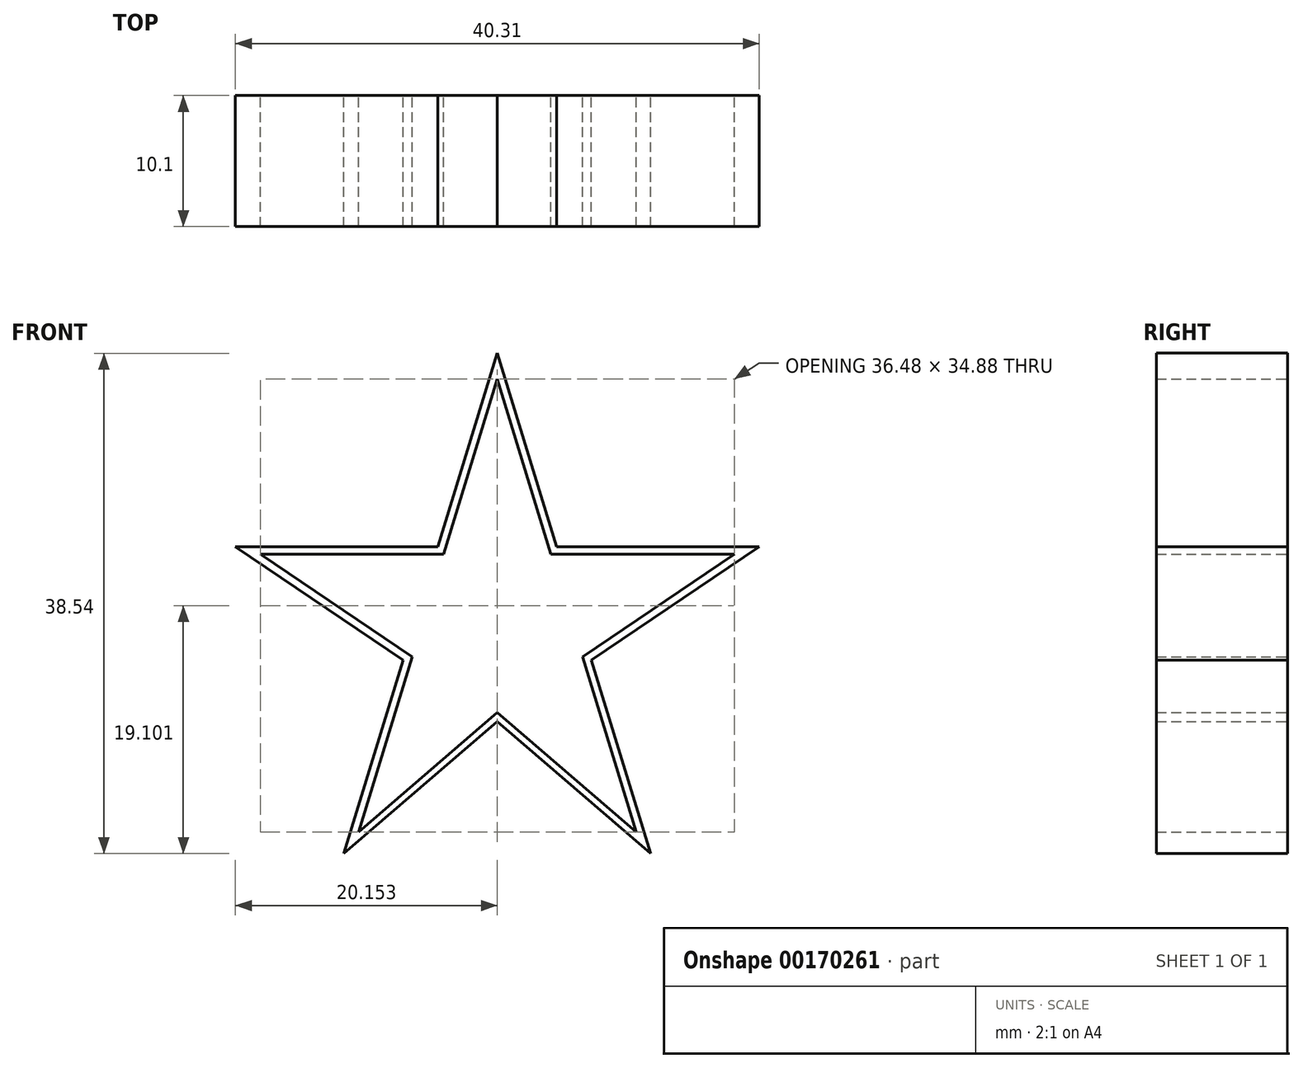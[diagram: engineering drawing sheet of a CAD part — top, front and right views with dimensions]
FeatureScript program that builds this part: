
annotation { "Feature Type Name" : "Feature", "Feature Type Description" : "" }
export const myFeature = defineFeature(function(context is Context, id is Id, definition is map)
    precondition{}
    {
        {
            var Q0;
            Q0=qCreatedBy(makeId("Front.planeOp"),FACE);
            var sketch = newSketch(context, id + "F0", { "sketchPlane" : qUnion([Q0])});
            skLineSegment(sketch, "E0", {"start": v(-37.38, 63.45) * mm, "end": v(-37.38, 61.45) * mm});
            skLineSegment(sketch, "E1", {"start": v(-37.38, 63.45) * mm, "end": v(-41.94, 48.55) * mm});
            skLineSegment(sketch, "E2", {"start": v(-37.38, 61.45) * mm, "end": v(-41.5, 47.96) * mm});
            skLineSegment(sketch, "E3", {"start": v(-41.94, 48.55) * mm, "end": v(-41.5, 47.96) * mm});
            skLineSegment(sketch, "E4", {"start": v(-41.94, 48.55) * mm, "end": v(-57.53, 48.55) * mm});
            skLineSegment(sketch, "E5", {"start": v(-55.62, 47.96) * mm, "end": v(-41.5, 47.96) * mm});
            skLineSegment(sketch, "E6", {"start": v(-49.74, 48.55) * mm, "end": v(-49.74, 47.96) * mm});
            skLineSegment(sketch, "E7", {"start": v(-39.66, 56) * mm, "end": v(-39.1, 55.83) * mm});
            skLineSegment(sketch, "E8", {"start": v(-55.62, 47.96) * mm, "end": v(-57.53, 48.55) * mm});
            skLineSegment(sketch, "E9.MirrorCS", {"start": v(-55.62, 47.96) * mm, "end": v(-43.93, 40.06) * mm});
            skLineSegment(sketch, "E10.MirrorCS", {"start": v(-44.62, 39.82) * mm, "end": v(-57.53, 48.55) * mm});
            skLineSegment(sketch, "E11.MirrorCS", {"start": v(-51.07, 44.18) * mm, "end": v(-50.75, 44.67) * mm});
            skLineSegment(sketch, "E12.MirrorCS", {"start": v(-44.62, 39.82) * mm, "end": v(-43.93, 40.06) * mm});
            skLineSegment(sketch, "E13.MirrorCS", {"start": v(-49.18, 24.91) * mm, "end": v(-44.62, 39.82) * mm});
            skLineSegment(sketch, "E14.MirrorCS", {"start": v(-48.06, 26.57) * mm, "end": v(-43.93, 40.06) * mm});
            skLineSegment(sketch, "E15", {"start": v(-49.18, 24.91) * mm, "end": v(-37.38, 35.1) * mm});
            skLineSegment(sketch, "E16.MirrorCS", {"start": v(-46.9, 32.37) * mm, "end": v(-46.34, 32.2) * mm});
            skLineSegment(sketch, "E17.MirrorCS", {"start": v(-49.18, 24.91) * mm, "end": v(-48.06, 26.57) * mm});
            skLineSegment(sketch, "E18", {"start": v(-37.38, 61.45) * mm, "end": v(-37.38, 35.1) * mm});
            skLineSegment(sketch, "E19", {"start": v(-48.06, 26.57) * mm, "end": v(-37.38, 35.79) * mm});
            skLineSegment(sketch, "E20", {"start": v(-42.4, 30.76) * mm, "end": v(-42.74, 31.16) * mm});
            skLineSegment(sketch, "E21.MirrorCS", {"start": v(-19.14, 47.96) * mm, "end": v(-17.22, 48.55) * mm});
            skLineSegment(sketch, "E22.MirrorCS", {"start": v(-25.57, 24.91) * mm, "end": v(-26.7, 26.57) * mm});
            skLineSegment(sketch, "E23.MirrorCS", {"start": v(-32.81, 48.55) * mm, "end": v(-33.25, 47.96) * mm});
            skLineSegment(sketch, "E24.MirrorCS", {"start": v(-30.14, 39.82) * mm, "end": v(-30.83, 40.06) * mm});
            skLineSegment(sketch, "E25.MirrorCS", {"start": v(-27.86, 32.37) * mm, "end": v(-28.42, 32.2) * mm});
            skLineSegment(sketch, "E26.MirrorCS", {"start": v(-35.1, 56) * mm, "end": v(-35.65, 55.83) * mm});
            skLineSegment(sketch, "E27.MirrorCS", {"start": v(-32.36, 30.76) * mm, "end": v(-32.01, 31.16) * mm});
            skLineSegment(sketch, "E28.MirrorCS", {"start": v(-25.02, 48.55) * mm, "end": v(-25.02, 47.96) * mm});
            skLineSegment(sketch, "E29.MirrorCS", {"start": v(-23.68, 44.18) * mm, "end": v(-24, 44.67) * mm});
            skLineSegment(sketch, "E30.MirrorCS", {"start": v(-19.14, 47.96) * mm, "end": v(-33.25, 47.96) * mm});
            skLineSegment(sketch, "E31.MirrorCS", {"start": v(-26.7, 26.57) * mm, "end": v(-37.38, 35.79) * mm});
            skLineSegment(sketch, "E32.MirrorCS", {"start": v(-26.7, 26.57) * mm, "end": v(-30.83, 40.06) * mm});
            skLineSegment(sketch, "E33.MirrorCS", {"start": v(-30.14, 39.82) * mm, "end": v(-17.22, 48.55) * mm});
            skLineSegment(sketch, "E34.MirrorCS", {"start": v(-37.38, 61.45) * mm, "end": v(-33.25, 47.96) * mm});
            skLineSegment(sketch, "E35.MirrorCS", {"start": v(-32.81, 48.55) * mm, "end": v(-17.22, 48.55) * mm});
            skLineSegment(sketch, "E36.MirrorCS", {"start": v(-19.14, 47.96) * mm, "end": v(-30.83, 40.06) * mm});
            skLineSegment(sketch, "E37.MirrorCS", {"start": v(-25.57, 24.91) * mm, "end": v(-30.14, 39.82) * mm});
            skLineSegment(sketch, "E38.MirrorCS", {"start": v(-25.57, 24.91) * mm, "end": v(-37.38, 35.1) * mm});
            skLineSegment(sketch, "E39.MirrorCS", {"start": v(-37.38, 63.45) * mm, "end": v(-32.81, 48.55) * mm});
            skSolve(sketch);
        }
        {
            var Q0;
            {var subQ1=sQuery(id+"F0.wireOp",EDGE,"E2");var subQ13=makeQuery(id+"F0.imprint","INTERSECT",VERTEX,{"derivedFrom":[subQ1,sQuery(id+"F0.wireOp",EDGE,"E7")]});Q0=makeQuery(id+"F0.imprint","IMPRINT",FACE,{"disambiguationData":[TD([[makeQuery(id+"F0.imprint","IMPRINT",EDGE,{"disambiguationData":[TD([[subQ13,-1.0]])],"derivedFrom":subQ1}),1.0]])]});}
            var Q1;
            {var subQ1=sQuery(id+"F0.wireOp",EDGE,"E30.MirrorCS");var subQ10=makeQuery(id+"F0.imprint","INTERSECT",VERTEX,{"derivedFrom":[sQuery(id+"F0.wireOp",EDGE,"E28.MirrorCS"),subQ1]});Q1=makeQuery(id+"F0.imprint","IMPRINT",FACE,{"disambiguationData":[TD([[makeQuery(id+"F0.imprint","IMPRINT",EDGE,{"disambiguationData":[TD([[subQ10,1.0]])],"derivedFrom":subQ1}),1.0]])]});}
            extrude(context, id + "F1", {"entities" : qUnion([Q0, Q1]), "depth" : 10.1 * mm});
        }
        {
            var Q0;
            {var subQ0=sQuery(id+"F0.wireOp",EDGE,"E21.MirrorCS");Q0=makeQuery(id+"F0.imprint","IMPRINT",FACE,{"disambiguationData":[TD([[makeQuery(id+"F0.imprint","IMPRINT",EDGE,{"derivedFrom":subQ0}),-1.0]])]});}
            var Q1;
            {var subQ0=sQuery(id+"F0.wireOp",EDGE,"E24.MirrorCS");Q1=makeQuery(id+"F0.imprint","IMPRINT",FACE,{"disambiguationData":[TD([[makeQuery(id+"F0.imprint","IMPRINT",EDGE,{"derivedFrom":subQ0}),-1.0]])]});}
            var Q2;
            {var subQ0=sQuery(id+"F0.wireOp",EDGE,"E22.MirrorCS");Q2=makeQuery(id+"F0.imprint","IMPRINT",FACE,{"disambiguationData":[TD([[makeQuery(id+"F0.imprint","IMPRINT",EDGE,{"derivedFrom":subQ0}),1.0]])]});}
            var Q3;
            {var subQ0=sQuery(id+"F0.wireOp",EDGE,"E22.MirrorCS");Q3=makeQuery(id+"F0.imprint","IMPRINT",FACE,{"disambiguationData":[TD([[makeQuery(id+"F0.imprint","IMPRINT",EDGE,{"derivedFrom":subQ0}),-1.0]])]});}
            var Q4;
            {var subQ0=sQuery(id+"F0.wireOp",EDGE,"E23.MirrorCS");Q4=makeQuery(id+"F0.imprint","IMPRINT",FACE,{"disambiguationData":[TD([[makeQuery(id+"F0.imprint","IMPRINT",EDGE,{"derivedFrom":subQ0}),-1.0]])]});}
            var Q5;
            {var subQ0=sQuery(id+"F0.wireOp",EDGE,"E0");Q5=makeQuery(id+"F0.imprint","IMPRINT",FACE,{"disambiguationData":[TD([[makeQuery(id+"F0.imprint","IMPRINT",EDGE,{"derivedFrom":subQ0}),-1.0]])]});}
            var Q6;
            {var subQ0=sQuery(id+"F0.wireOp",EDGE,"E0");Q6=makeQuery(id+"F0.imprint","IMPRINT",FACE,{"disambiguationData":[TD([[makeQuery(id+"F0.imprint","IMPRINT",EDGE,{"derivedFrom":subQ0}),1.0]])]});}
            var Q7;
            {var subQ0=sQuery(id+"F0.wireOp",EDGE,"E3");Q7=makeQuery(id+"F0.imprint","IMPRINT",FACE,{"disambiguationData":[TD([[makeQuery(id+"F0.imprint","IMPRINT",EDGE,{"derivedFrom":subQ0}),1.0]])]});}
            var Q8;
            {var subQ0=sQuery(id+"F0.wireOp",EDGE,"E8");Q8=makeQuery(id+"F0.imprint","IMPRINT",FACE,{"disambiguationData":[TD([[makeQuery(id+"F0.imprint","IMPRINT",EDGE,{"derivedFrom":subQ0}),1.0]])]});}
            var Q9;
            {var subQ2=sQuery(id+"F0.wireOp",EDGE,"E11.MirrorCS");Q9=makeQuery(id+"F0.imprint","IMPRINT",FACE,{"disambiguationData":[TD([[makeQuery(id+"F0.imprint","IMPRINT",EDGE,{"derivedFrom":subQ2}),-1.0]])]});}
            var Q10;
            {var subQ0=sQuery(id+"F0.wireOp",EDGE,"E12.MirrorCS");Q10=makeQuery(id+"F0.imprint","IMPRINT",FACE,{"disambiguationData":[TD([[makeQuery(id+"F0.imprint","IMPRINT",EDGE,{"derivedFrom":subQ0}),-1.0]])]});}
            var Q11;
            {var subQ2=sQuery(id+"F0.wireOp",EDGE,"E16.MirrorCS");Q11=makeQuery(id+"F0.imprint","IMPRINT",FACE,{"disambiguationData":[TD([[makeQuery(id+"F0.imprint","IMPRINT",EDGE,{"derivedFrom":subQ2}),-1.0]])]});}
            var Q12;
            {var subQ0=sQuery(id+"F0.wireOp",EDGE,"E17.MirrorCS");Q12=makeQuery(id+"F0.imprint","IMPRINT",FACE,{"disambiguationData":[TD([[makeQuery(id+"F0.imprint","IMPRINT",EDGE,{"derivedFrom":subQ0}),-1.0]])]});}
            var Q13;
            {var subQ3=sQuery(id+"F0.wireOp",EDGE,"E20");Q13=makeQuery(id+"F0.imprint","IMPRINT",FACE,{"disambiguationData":[TD([[makeQuery(id+"F0.imprint","IMPRINT",EDGE,{"derivedFrom":subQ3}),-1.0]])]});}
            var Q14;
            {var subQ5=sQuery(id+"F0.wireOp",EDGE,"E27.MirrorCS");Q14=makeQuery(id+"F0.imprint","IMPRINT",FACE,{"disambiguationData":[TD([[makeQuery(id+"F0.imprint","IMPRINT",EDGE,{"derivedFrom":subQ5}),1.0]])]});}
            var Q15;
            {var subQ0=sQuery(id+"F0.wireOp",EDGE,"E24.MirrorCS");Q15=makeQuery(id+"F0.imprint","IMPRINT",FACE,{"disambiguationData":[TD([[makeQuery(id+"F0.imprint","IMPRINT",EDGE,{"derivedFrom":subQ0}),1.0]])]});}
            var Q16;
            {var subQ0=sQuery(id+"F0.wireOp",EDGE,"E3");Q16=makeQuery(id+"F0.imprint","IMPRINT",FACE,{"disambiguationData":[TD([[makeQuery(id+"F0.imprint","IMPRINT",EDGE,{"derivedFrom":subQ0}),-1.0]])]});}
            var Q17;
            {var subQ2=sQuery(id+"F0.wireOp",EDGE,"E6");Q17=makeQuery(id+"F0.imprint","IMPRINT",FACE,{"disambiguationData":[TD([[makeQuery(id+"F0.imprint","IMPRINT",EDGE,{"derivedFrom":subQ2}),-1.0]])]});}
            var Q18;
            {var subQ0=sQuery(id+"F0.wireOp",EDGE,"E21.MirrorCS");Q18=makeQuery(id+"F0.imprint","IMPRINT",FACE,{"disambiguationData":[TD([[makeQuery(id+"F0.imprint","IMPRINT",EDGE,{"derivedFrom":subQ0}),1.0]])]});}
            var Q19;
            {var subQ0=sQuery(id+"F0.wireOp",EDGE,"E23.MirrorCS");Q19=makeQuery(id+"F0.imprint","IMPRINT",FACE,{"disambiguationData":[TD([[makeQuery(id+"F0.imprint","IMPRINT",EDGE,{"derivedFrom":subQ0}),1.0]])]});}
            extrude(context, id + "F2", {"entities" : qUnion([Q0, Q1, Q2, Q3, Q4, Q5, Q6, Q7, Q8, Q9, Q10, Q11, Q12, Q13, Q14, Q15, Q16, Q17, Q18, Q19]), "depth" : 10.1 * mm});
        }
    });
